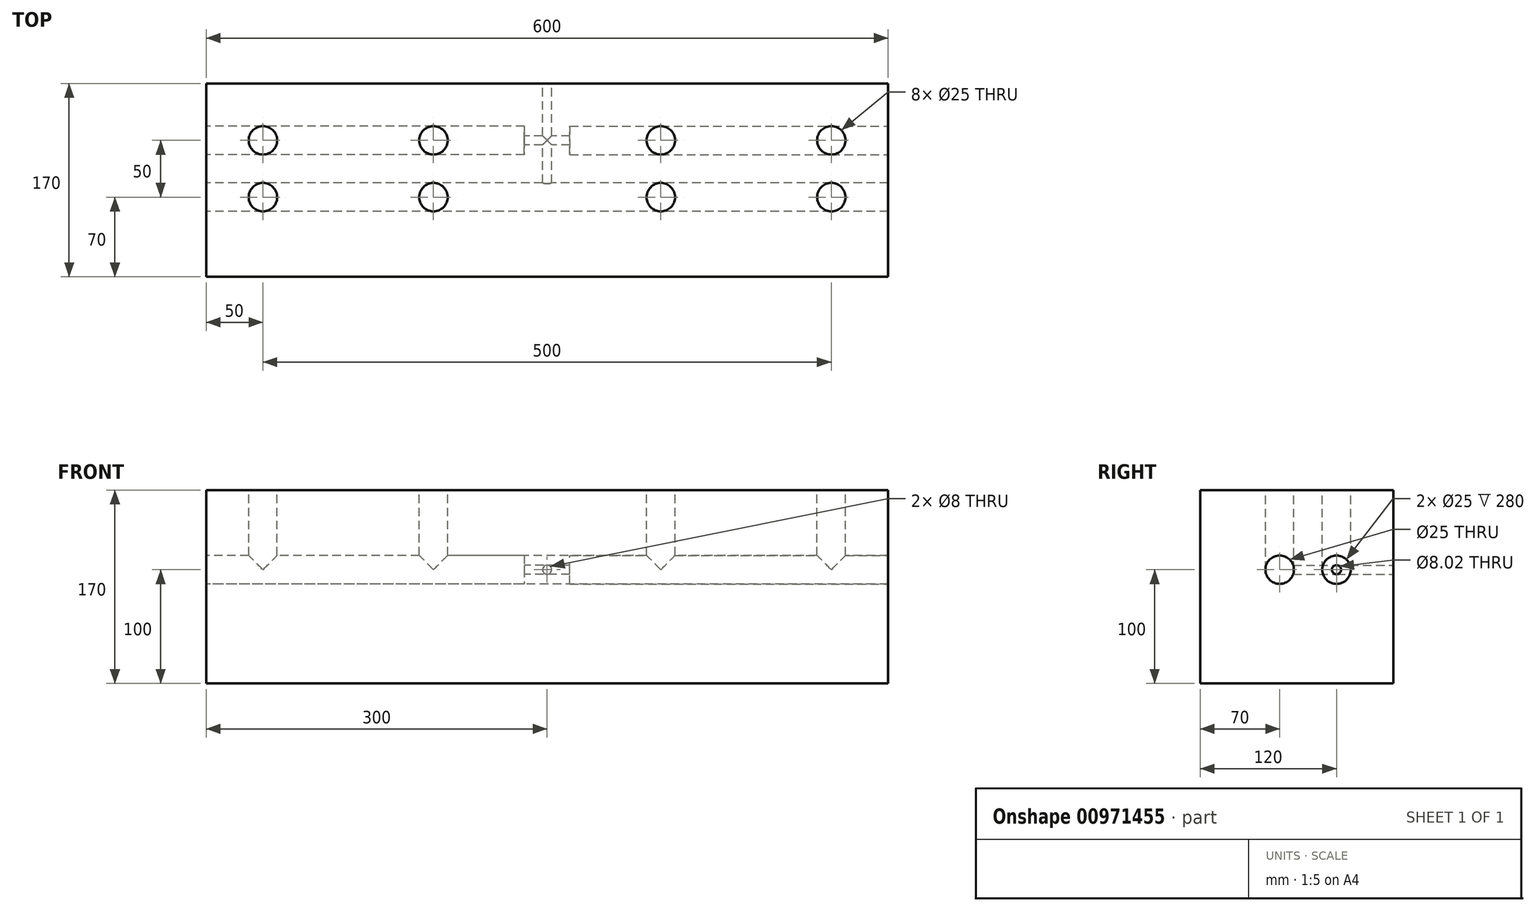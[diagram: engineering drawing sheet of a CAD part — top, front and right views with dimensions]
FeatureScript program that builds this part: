
annotation { "Feature Type Name" : "Feature", "Feature Type Description" : "" }
export const myFeature = defineFeature(function(context is Context, id is Id, definition is map)
    precondition{}
    {
        {
            var Q0;
            Q0=qCreatedBy(makeId("Right.planeOp"),FACE);
            var sketch = newSketch(context, id + "F0", { "sketchPlane" : qUnion([Q0])});
            skLineSegment(sketch, "E0.bottom", {"start": v(0, 0) * mm, "end": v(-170, 0) * mm});
            skLineSegment(sketch, "E0.top", {"start": v(0, 170) * mm, "end": v(-170, 170) * mm});
            skLineSegment(sketch, "E0.left", {"start": v(0, 0) * mm, "end": v(0, 170) * mm});
            skLineSegment(sketch, "E0.right", {"start": v(-170, 0) * mm, "end": v(-170, 170) * mm});
            skSolve(sketch);
        }
        {
            var Q0;
            Q0=makeQuery(id+"F0.imprint","IMPRINT",FACE,{"disambiguationData":[TD([[makeQuery(id+"F0.imprint","IMPRINT",EDGE,{"derivedFrom":sQuery(id+"F0.wireOp",EDGE,"E0.bottom")}),-1.0]])]});
            extrude(context, id + "F1", {"entities" : qUnion([Q0]), "depth" : 600 * mm, "offsetDistance" : 25 * mm});
        }
        {
            var Q0;
            Q0=makeQuery(id+"F1.opExtrude","CAP_FACE",FACE,{"disambiguationData":[OSD([sQuery(id+"F0.wireOp",EDGE,"E0.bottom"),sQuery(id+"F0.wireOp",EDGE,"E0.top"),sQuery(id+"F0.wireOp",EDGE,"E0.left"),sQuery(id+"F0.wireOp",EDGE,"E0.right")])],"isStart":true});
            var sketch = newSketch(context, id + "F2", { "sketchPlane" : qUnion([Q0])});
            skCircle(sketch, "E1", {"center": v(100, 100) * mm, "radius": 12.5 * mm});
            skCircle(sketch, "E2", {"center": v(50, 100) * mm, "radius": 12.5 * mm});
            skCircle(sketch, "E3", {"center": v(50, 100) * mm, "radius": 4 * mm});
            skSolve(sketch);
        }
        {
            var Q0;
            Q0=makeQuery(id+"F2.imprint","IMPRINT",FACE,{"disambiguationData":[TD([[makeQuery(id+"F2.imprint","IMPRINT",EDGE,{"derivedFrom":sQuery(id+"F2.wireOp",EDGE,"E2")}),1.0]])]});
            var Q1;
            Q1=makeQuery(id+"F2.imprint","IMPRINT",FACE,{"disambiguationData":[TD([[makeQuery(id+"F2.imprint","IMPRINT",EDGE,{"derivedFrom":sQuery(id+"F2.wireOp",EDGE,"E1")}),1.0]])]});
            extrude(context, id + "F3", {"entities" : qUnion([Q0, Q1]), "operationType" : NewBodyOperationType.REMOVE, "oppositeDirection" : true, "depth" : 280 * mm, "offsetDistance" : 25 * mm});
        }
        {
            var Q0;
            Q0=qCreatedBy(makeId("Right.planeOp"),FACE);
            cPlane(context, id + "F4", {"entities" : qUnion([Q0]), "cplaneType" : CPlaneType.OFFSET, "offset" : 600 * mm, "width" : 150 * mm, "height" : 150 * mm});
        }
        {
            var Q0;
            Q0=qCreatedBy(id+"F4.planeOp",FACE);
            var sketch = newSketch(context, id + "F5", { "sketchPlane" : qUnion([Q0])});
            skCircle(sketch, "E4", {"center": v(-50, 100) * mm, "radius": 12.5 * mm});
            skCircle(sketch, "E5", {"center": v(-100, 100) * mm, "radius": 12.5 * mm});
            skSolve(sketch);
        }
        {
            var Q0;
            Q0=makeQuery(id+"F5.imprint","IMPRINT",FACE,{"disambiguationData":[TD([[makeQuery(id+"F5.imprint","IMPRINT",EDGE,{"derivedFrom":sQuery(id+"F5.wireOp",EDGE,"E4")}),1.0]])]});
            var Q1;
            Q1=makeQuery(id+"F5.imprint","IMPRINT",FACE,{"disambiguationData":[TD([[makeQuery(id+"F5.imprint","IMPRINT",EDGE,{"derivedFrom":sQuery(id+"F5.wireOp",EDGE,"E5")}),1.0]])]});
            extrude(context, id + "F6", {"entities" : qUnion([Q0, Q1]), "operationType" : NewBodyOperationType.REMOVE, "oppositeDirection" : true, "depth" : 280 * mm, "offsetDistance" : 25 * mm});
        }
        {
            var Q0;
            Q0=makeQuery(id+"F1.opExtrude","SWEPT_FACE",FACE,{"disambiguationData":[OSD([sQuery(id+"F0.wireOp",EDGE,"E0.top")])]});
            var sketch = newSketch(context, id + "F7", { "sketchPlane" : qUnion([Q0])});
            skCircle(sketch, "E6", {"center": v(50, -50) * mm, "radius": 12.5 * mm});
            skCircle(sketch, "E7", {"center": v(200, -50) * mm, "radius": 12.5 * mm});
            skCircle(sketch, "E8", {"center": v(400, -50) * mm, "radius": 12.5 * mm});
            skCircle(sketch, "E9", {"center": v(550, -50) * mm, "radius": 12.5 * mm});
            skCircle(sketch, "E10", {"center": v(550, -100) * mm, "radius": 12.5 * mm});
            skCircle(sketch, "E11", {"center": v(400, -100) * mm, "radius": 12.5 * mm});
            skCircle(sketch, "E12", {"center": v(50, -100) * mm, "radius": 12.5 * mm});
            skCircle(sketch, "E13", {"center": v(200, -100) * mm, "radius": 12.5 * mm});
            skSolve(sketch);
        }
        {
            var Q0;
            Q0=makeQuery(id+"F7.imprint","IMPRINT",FACE,{"disambiguationData":[TD([[makeQuery(id+"F7.imprint","IMPRINT",EDGE,{"derivedFrom":sQuery(id+"F7.wireOp",EDGE,"E12")}),1.0]])]});
            var Q1;
            Q1=makeQuery(id+"F7.imprint","IMPRINT",FACE,{"disambiguationData":[TD([[makeQuery(id+"F7.imprint","IMPRINT",EDGE,{"derivedFrom":sQuery(id+"F7.wireOp",EDGE,"E13")}),1.0]])]});
            var Q2;
            Q2=makeQuery(id+"F7.imprint","IMPRINT",FACE,{"disambiguationData":[TD([[makeQuery(id+"F7.imprint","IMPRINT",EDGE,{"derivedFrom":sQuery(id+"F7.wireOp",EDGE,"E11")}),1.0]])]});
            var Q3;
            Q3=makeQuery(id+"F7.imprint","IMPRINT",FACE,{"disambiguationData":[TD([[makeQuery(id+"F7.imprint","IMPRINT",EDGE,{"derivedFrom":sQuery(id+"F7.wireOp",EDGE,"E10")}),1.0]])]});
            var Q4;
            Q4=makeQuery(id+"F7.imprint","IMPRINT",FACE,{"disambiguationData":[TD([[makeQuery(id+"F7.imprint","IMPRINT",EDGE,{"derivedFrom":sQuery(id+"F7.wireOp",EDGE,"E9")}),1.0]])]});
            var Q5;
            Q5=makeQuery(id+"F7.imprint","IMPRINT",FACE,{"disambiguationData":[TD([[makeQuery(id+"F7.imprint","IMPRINT",EDGE,{"derivedFrom":sQuery(id+"F7.wireOp",EDGE,"E8")}),1.0]])]});
            var Q6;
            Q6=makeQuery(id+"F7.imprint","IMPRINT",FACE,{"disambiguationData":[TD([[makeQuery(id+"F7.imprint","IMPRINT",EDGE,{"derivedFrom":sQuery(id+"F7.wireOp",EDGE,"E7")}),1.0]])]});
            var Q7;
            Q7=makeQuery(id+"F7.imprint","IMPRINT",FACE,{"disambiguationData":[TD([[makeQuery(id+"F7.imprint","IMPRINT",EDGE,{"derivedFrom":sQuery(id+"F7.wireOp",EDGE,"E6")}),1.0]])]});
            var Q8;
            Q8=sQuery(id+"F7.wireOp",EDGE,"E12");
            var Q9;
            Q9=sQuery(id+"F7.wireOp",EDGE,"E6");
            var Q10;
            Q10=sQuery(id+"F7.wireOp",EDGE,"E13");
            var Q11;
            Q11=sQuery(id+"F7.wireOp",EDGE,"E7");
            var Q12;
            Q12=sQuery(id+"F7.wireOp",EDGE,"E8");
            var Q13;
            Q13=sQuery(id+"F7.wireOp",EDGE,"E9");
            var Q14;
            Q14=sQuery(id+"F7.wireOp",EDGE,"E10");
            var Q15;
            Q15=sQuery(id+"F7.wireOp",EDGE,"E11");
            extrude(context, id + "F8", {"entities" : qUnion([Q0, Q1, Q2, Q3, Q4, Q5, Q6, Q7]), "operationType" : NewBodyOperationType.REMOVE, "surfaceEntities" : qUnion([Q8, Q9, Q10, Q11, Q12, Q13, Q14, Q15]), "oppositeDirection" : true, "depth" : 70 * mm, "offsetDistance" : 25 * mm});
        }
        {
            var Q0;
            Q0=makeQuery(id+"F3.boolean.opBoolean","SPLIT",FACE,{"disambiguationData":[TD([makeQuery(id+"F3.opExtrude","SWEPT_FACE",FACE,{"disambiguationData":[OSD([sQuery(id+"F2.wireOp",EDGE,"E3")])]})])],"derivedFrom":makeQuery(id+"F1.opExtrude","CAP_FACE",FACE,{"disambiguationData":[OSD([sQuery(id+"F0.wireOp",EDGE,"E0.bottom"),sQuery(id+"F0.wireOp",EDGE,"E0.top"),sQuery(id+"F0.wireOp",EDGE,"E0.left"),sQuery(id+"F0.wireOp",EDGE,"E0.right")])],"isStart":true})});
            var Q1;
            Q1=makeQuery(id+"F3.boolean.opBoolean","SPLIT",FACE,{"disambiguationData":[TD([makeQuery(id+"F3.opExtrude","SWEPT_FACE",FACE,{"disambiguationData":[OSD([sQuery(id+"F2.wireOp",EDGE,"qixCw0Jy-Cxsl-SWU7-l0oz-FYMAdKhViwOn")])]})])],"derivedFrom":makeQuery(id+"F1.opExtrude","CAP_FACE",FACE,{"disambiguationData":[OSD([sQuery(id+"F0.wireOp",EDGE,"E0.bottom"),sQuery(id+"F0.wireOp",EDGE,"E0.top"),sQuery(id+"F0.wireOp",EDGE,"E0.left"),sQuery(id+"F0.wireOp",EDGE,"E0.right")])],"isStart":true})});
            extrude(context, id + "F9", {"entities" : qUnion([Q0, Q1]), "operationType" : NewBodyOperationType.REMOVE, "oppositeDirection" : true, "depth" : 600 * mm, "offsetDistance" : 25 * mm});
        }
        {
            var Q0;
            Q0=makeQuery(id+"F1.opExtrude","SWEPT_FACE",FACE,{"disambiguationData":[OSD([sQuery(id+"F0.wireOp",EDGE,"E0.left")])]});
            var sketch = newSketch(context, id + "F10", { "sketchPlane" : qUnion([Q0])});
            skCircle(sketch, "E14", {"center": v(-300, 100) * mm, "radius": 4 * mm});
            skSolve(sketch);
        }
        {
            var Q0;
            Q0=makeQuery(id+"F10.imprint","IMPRINT",FACE,{"disambiguationData":[TD([[makeQuery(id+"F10.imprint","IMPRINT",EDGE,{"derivedFrom":sQuery(id+"F10.wireOp",EDGE,"E14")}),1.0]])]});
            extrude(context, id + "F11", {"entities" : qUnion([Q0]), "operationType" : NewBodyOperationType.REMOVE, "oppositeDirection" : true, "depth" : 100 * mm, "offsetDistance" : 25 * mm});
        }
        {
            var Q0;
            Q0=makeQuery(id+"F3.boolean.opBoolean","COPY",FACE,{"derivedFrom":makeQuery(id+"F3.opExtrude","CAP_FACE",FACE,{"disambiguationData":[OSD([sQuery(id+"F2.wireOp",EDGE,"E1")])],"isStart":false})});
            extrude(context, id + "F12", {"entities" : qUnion([Q0]), "operationType" : NewBodyOperationType.REMOVE, "oppositeDirection" : true, "depth" : 50 * mm, "offsetDistance" : 25 * mm});
        }
    });
